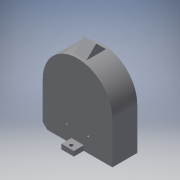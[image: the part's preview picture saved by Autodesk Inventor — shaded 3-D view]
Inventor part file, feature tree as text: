
AUTODESK INVENTOR PART (.ipt)
format: ipt  version: 2016 (Build 200138000, 138)  size: 164,352 bytes
history: native  units: in
note: dims shown in document units (in); Inventor stores cm internally (conversion verified against a paired STEP export)
features: extrude x7, sketch x7, reference x4, plane x1
ambient origin geometry x8: Origin, YZ Plane, XZ Plane, XY Plane, X Axis, Y Axis, Z Axis, Center Point
bodies: Solid1 (feature_tree)
feature tree (19):
  extrude  "Extrusion1"  Depth=1.0in TaperAngle=0.0deg
  extrude  "Extrusion2"  Depth=0.4in TaperAngle=0.0deg
  extrude  "Extrusion4"  Depth=0.1065in
  plane  "Work Plane1"
  extrude  "Extrusion7"  Depth=0.394in
  extrude  "Extrusion9"  Depth=0.5in TaperAngle=0.0deg
  extrude  "Extrusion10"  Depth=0.5in
  extrude  "Extrusion11"  Depth=1.0in
  sketch  "Sketch1"  dims[d0=2.8in d1=1.0in d2=0.0in]
  reference  "Reference1"
  sketch  "Sketch2"  dims[d4=0.4in d5=0.0in d13=0.4in d14=0.0in]
  reference  "Reference2"
  sketch  "Sketch4"  dims[d26=-1.4in d27=0.1065in]
  sketch  "Sketch7"  dims[d28=0.787in d29=0.394in]
  sketch  "Sketch9"  dims[d30=0.394in d31=0.5in d32=0.0in]
  sketch  "Sketch10"  dims[d39=0.25in d40=0.5in]
  sketch  "Sketch11"  dims[d41=0.15in d42=0.138in d43=1.0in d44=0.0in d45=0.25in d46=0.5in d47=0.15in d48=0.177in d49=1.0in d50=0.0in d51=0.5in d52=0.5in d53=0.0394in d54=0.098in d55=0.0394in d56=0.098in d57=1.0in d58=0.0in]
  reference  "Reference3"
  reference  "Reference4"
